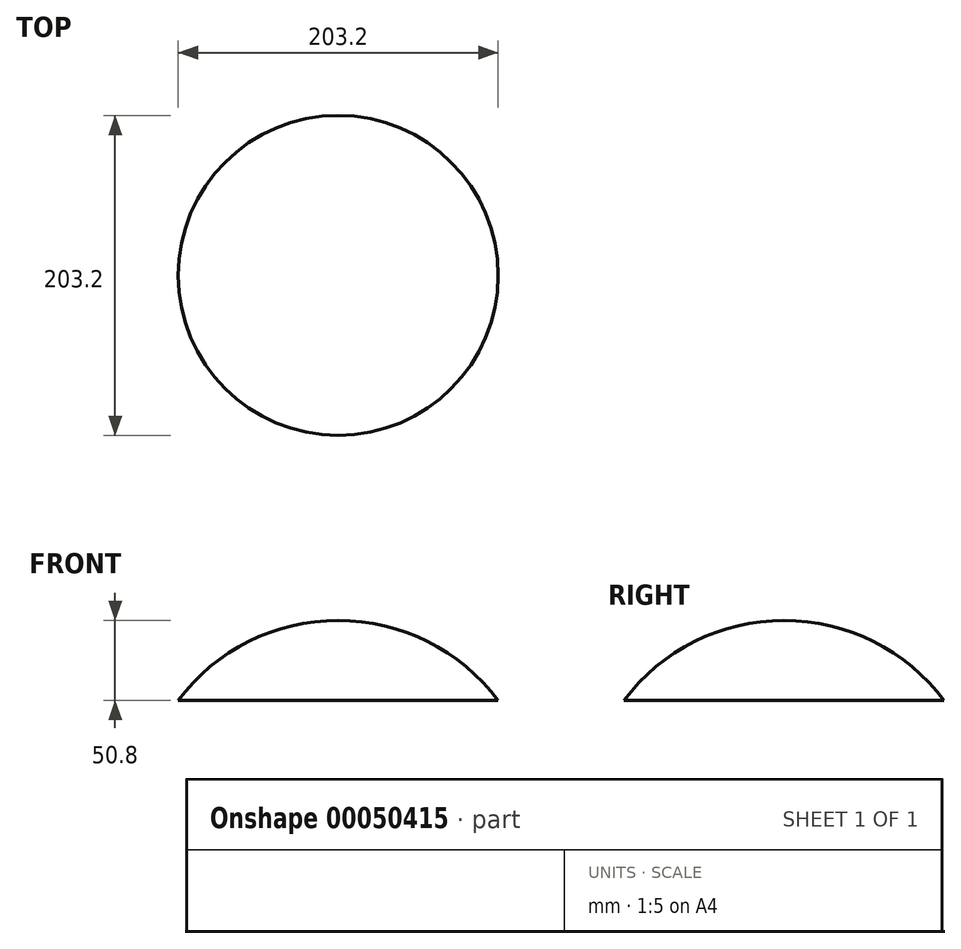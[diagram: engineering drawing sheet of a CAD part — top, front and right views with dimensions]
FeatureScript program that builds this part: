
annotation { "Feature Type Name" : "Feature", "Feature Type Description" : "" }
export const myFeature = defineFeature(function(context is Context, id is Id, definition is map)
    precondition{}
    {
        {
            var Q0;
            Q0=qCreatedBy(makeId("Top.planeOp"),FACE);
            var sketch = newSketch(context, id + "F0", { "sketchPlane" : qUnion([Q0])});
            skCircle(sketch, "E0", {"center": v(0, 0) * mm, "radius": 127 * mm});
            skLineSegment(sketch, "E1", {"start": v(-81.25, 97.61) * mm, "end": v(0, 0) * mm});
            skLineSegment(sketch, "E2", {"start": v(0, 0) * mm, "end": v(81.25, -97.61) * mm});
            skSolve(sketch);
        }
        {
            var Q0;
            {var subQ0=sQuery(id+"F0.wireOp",EDGE,"E1");Q0=makeQuery(id+"F0.imprint","IMPRINT",FACE,{"disambiguationData":[TD([[makeQuery(id+"F0.imprint","IMPRINT",EDGE,{"derivedFrom":subQ0}),1.0]])]});}
            var Q1;
            Q1=sQuery(id+"F0.wireOp",EDGE,"E2");
            revolve(context, id + "F1", {"entities" : qUnion([Q0]), "axis" : qUnion([Q1]), "revolveType" : RevolveType.FULL});
        }
        {
            var Q0;
            Q0=qCreatedBy(makeId("Top.planeOp"),FACE);
            cPlane(context, id + "F2", {"entities" : qUnion([Q0]), "cplaneType" : CPlaneType.OFFSET, "offset" : 76.2 * mm, "width" : 152.4 * mm, "height" : 152.4 * mm});
        }
        {
            var Q0;
            Q0=qCreatedBy(id+"F2.planeOp",FACE);
            var sketch = newSketch(context, id + "F3", { "sketchPlane" : qUnion([Q0])});
            skLineSegment(sketch, "E3.rect.bottom", {"start": v(127, -127) * mm, "end": v(-127, -127) * mm});
            skLineSegment(sketch, "E3.rect.top", {"start": v(127, 127) * mm, "end": v(-127, 127) * mm});
            skLineSegment(sketch, "E3.rect.left", {"start": v(127, -127) * mm, "end": v(127, 127) * mm});
            skLineSegment(sketch, "E3.rect.right", {"start": v(-127, -127) * mm, "end": v(-127, 127) * mm});
            skPoint(sketch, "E3.rect.middle", {"position": v(0, 0) * mm});
            skSolve(sketch);
        }
        {
            var Q0;
            Q0=makeQuery(id+"F3.imprint","IMPRINT",FACE,{"disambiguationData":[TD([[makeQuery(id+"F3.imprint","IMPRINT",EDGE,{"derivedFrom":sQuery(id+"F3.wireOp",EDGE,"E3.rect.bottom")}),-1.0]])]});
            extrude(context, id + "F4", {"entities" : qUnion([Q0]), "operationType" : NewBodyOperationType.REMOVE, "oppositeDirection" : true, "depth" : 217.12 * mm});
        }
    });
